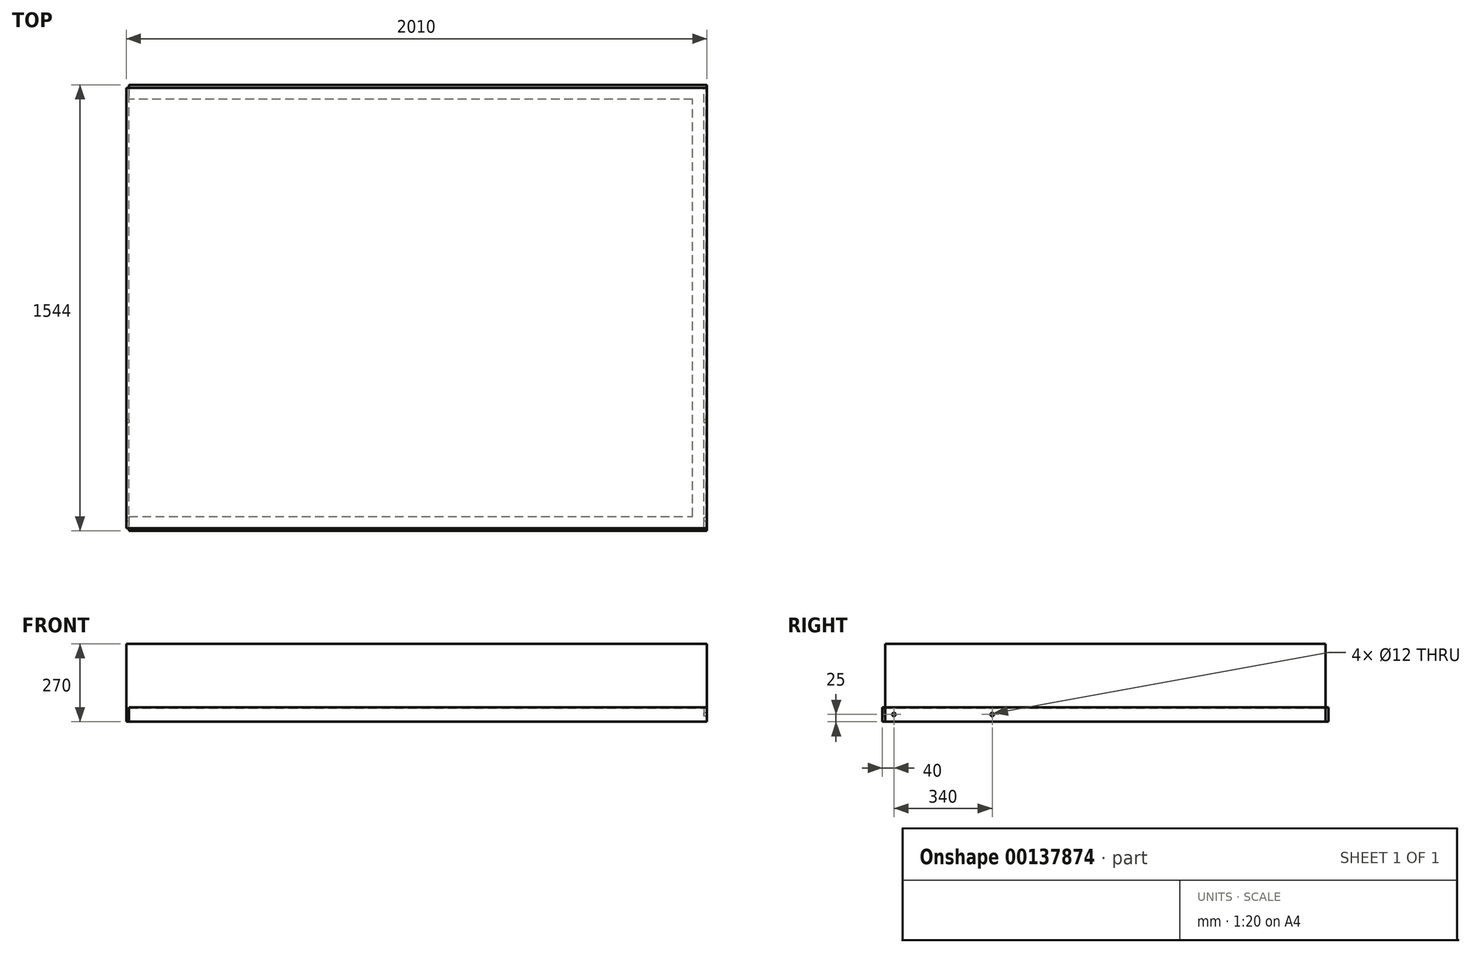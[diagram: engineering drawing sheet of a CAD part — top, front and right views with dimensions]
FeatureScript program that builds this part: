
annotation { "Feature Type Name" : "Feature", "Feature Type Description" : "" }
export const myFeature = defineFeature(function(context is Context, id is Id, definition is map)
    precondition{}
    {
        {
            var Q0;
            Q0=qCreatedBy(makeId("Top.planeOp"),FACE);
            var sketch = newSketch(context, id + "F0", { "sketchPlane" : qUnion([Q0])});
            skLineSegment(sketch, "E0.bottom", {"start": v(0, 0) * mm, "end": v(-2000, 0) * mm});
            skLineSegment(sketch, "E0.top", {"start": v(0, 1524) * mm, "end": v(-2000, 1524) * mm});
            skLineSegment(sketch, "E0.left", {"start": v(0, 0) * mm, "end": v(0, 1524) * mm});
            skLineSegment(sketch, "E0.right", {"start": v(-2000, 0) * mm, "end": v(-2000, 1524) * mm});
            skSolve(sketch);
        }
        {
            var Q0;
            Q0 = qSketchRegion(id + "F0", true);
            extrude(context, id + "F1", {"entities" : qUnion([Q0]), "depth" : 220 * mm});
        }
        {
            var Q0;
            Q0=makeQuery(id+"F1.opExtrude","SWEPT_FACE",FACE,{"disambiguationData":[OSD([sQuery(id+"F0.wireOp",EDGE,"E0.left")])]});
            var sketch = newSketch(context, id + "F2", { "sketchPlane" : qUnion([Q0])});
            skLineSegment(sketch, "E1", {"start": v(0, 220) * mm, "end": v(0, -50) * mm});
            skLineSegment(sketch, "E2", {"start": v(0, -50) * mm, "end": v(1524, -50) * mm});
            skLineSegment(sketch, "E3", {"start": v(1524, -50) * mm, "end": v(1524, 220) * mm});
            skLineSegment(sketch, "E4", {"start": v(1524, 220) * mm, "end": v(0, 220) * mm});
            skSolve(sketch);
        }
        {
            var Q0;
            Q0 = qSketchRegion(id + "F2", true);
            extrude(context, id + "F3", {"entities" : qUnion([Q0]), "operationType" : NewBodyOperationType.ADD, "oppositeDirection" : true, "depth" : 10 * mm});
        }
        {
            var Q0;
            Q0=makeQuery(id+"F1.opExtrude","SWEPT_FACE",FACE,{"disambiguationData":[OSD([sQuery(id+"F0.wireOp",EDGE,"E0.right")])]});
            var sketch = newSketch(context, id + "F4", { "sketchPlane" : qUnion([Q0])});
            skLineSegment(sketch, "E5", {"start": v(-1524, 220) * mm, "end": v(-1524, -50) * mm});
            skLineSegment(sketch, "E6", {"start": v(-1524, -50) * mm, "end": v(0, -50) * mm});
            skLineSegment(sketch, "E7", {"start": v(0, -50) * mm, "end": v(0, 220) * mm});
            skLineSegment(sketch, "E8", {"start": v(0, 220) * mm, "end": v(-1524, 220) * mm});
            skSolve(sketch);
        }
        {
            var Q0;
            Q0 = qSketchRegion(id + "F4", true);
            extrude(context, id + "F5", {"entities" : qUnion([Q0]), "operationType" : NewBodyOperationType.ADD, "depth" : 10 * mm});
        }
        {
            var Q0;
            Q0=makeQuery(id+"F3.boolean.opBoolean","MERGE",FACE,{"derivedFrom":[makeQuery(id+"F1.opExtrude","SWEPT_FACE",FACE,{"disambiguationData":[OSD([sQuery(id+"F0.wireOp",EDGE,"E0.left")])]}),makeQuery(id+"F3.opExtrude","CAP_FACE",FACE,{"disambiguationData":[OSD([sQuery(id+"F2.wireOp",EDGE,"E1"),sQuery(id+"F2.wireOp",EDGE,"E2"),sQuery(id+"F2.wireOp",EDGE,"E3"),sQuery(id+"F2.wireOp",EDGE,"E4")])],"isStart":true})]});
            var sketch = newSketch(context, id + "F6", { "sketchPlane" : qUnion([Q0])});
            skPoint(sketch, "E9", {"position": v(30, -25) * mm});
            skPoint(sketch, "E10", {"position": v(370, -25) * mm});
            skSolve(sketch);
        }
        {
            var Q0;
            Q0=sQuery(id+"F6.wireOp",VERTEX,"E9");
            var Q1;
            Q1=makeQuery(id+"F1.opExtrude","SWEPT_BODY",BODY,{"disambiguationData":[OSD([sQuery(id+"F0.wireOp",EDGE,"E0.bottom"),sQuery(id+"F0.wireOp",EDGE,"E0.top"),sQuery(id+"F0.wireOp",EDGE,"E0.left"),sQuery(id+"F0.wireOp",EDGE,"E0.right")])]});
            hole(context, id + "F7", {"style" : HoleStyle.SIMPLE, "endStyle" : HoleEndStyle.THROUGH, "holeDiameter" : 12 * mm, "locations" : qUnion([Q0]), "scope" : qUnion([Q1]), "isTappedThrough" : true, "startStyle" : HoleStartStyle.PART});
        }
        {
            var Q0;
            Q0=sQuery(id+"F6.wireOp",VERTEX,"E10");
            var Q1;
            Q1=makeQuery(id+"F1.opExtrude","SWEPT_BODY",BODY,{"disambiguationData":[OSD([sQuery(id+"F0.wireOp",EDGE,"E0.bottom"),sQuery(id+"F0.wireOp",EDGE,"E0.top"),sQuery(id+"F0.wireOp",EDGE,"E0.left"),sQuery(id+"F0.wireOp",EDGE,"E0.right")])]});
            hole(context, id + "F8", {"style" : HoleStyle.SIMPLE, "endStyle" : HoleEndStyle.THROUGH, "holeDiameter" : 12 * mm, "locations" : qUnion([Q0]), "scope" : qUnion([Q1]), "isTappedThrough" : true, "startStyle" : HoleStartStyle.PART});
        }
        {
            var Q0;
            Q0=qCreatedBy(makeId("Front.planeOp"),FACE);
            var sketch = newSketch(context, id + "F9", { "sketchPlane" : qUnion([Q0])});
            skLineSegment(sketch, "E11", {"start": v(0, 0) * mm, "end": v(-50, 0) * mm});
            skLineSegment(sketch, "E12", {"start": v(-50, 0) * mm, "end": v(-50, -3) * mm});
            skLineSegment(sketch, "E13", {"start": v(-50, -3) * mm, "end": v(-3, -3) * mm});
            skLineSegment(sketch, "E14", {"start": v(-3, -3) * mm, "end": v(-3, -50) * mm});
            skLineSegment(sketch, "E15", {"start": v(-3, -50) * mm, "end": v(0, -50) * mm});
            skLineSegment(sketch, "E16", {"start": v(0, -50) * mm, "end": v(0, 0) * mm});
            skSolve(sketch);
        }
        {
            var Q0;
            Q0 = qSketchRegion(id + "F9", true);
            var Q1;
            Q1=makeQuery(id+"F3.boolean.opBoolean","INTERSECT",EDGE,{"derivedFrom":[makeQuery(id+"F1.opExtrude","CAP_FACE",FACE,{"disambiguationData":[OSD([sQuery(id+"F0.wireOp",EDGE,"E0.bottom"),sQuery(id+"F0.wireOp",EDGE,"E0.top"),sQuery(id+"F0.wireOp",EDGE,"E0.left"),sQuery(id+"F0.wireOp",EDGE,"E0.right")])],"isStart":true}),makeQuery(id+"F3.opExtrude","CAP_FACE",FACE,{"disambiguationData":[OSD([sQuery(id+"F2.wireOp",EDGE,"E1"),sQuery(id+"F2.wireOp",EDGE,"E2"),sQuery(id+"F2.wireOp",EDGE,"E3"),sQuery(id+"F2.wireOp",EDGE,"E4")])],"isStart":false})]});
            var Q2;
            Q2=makeQuery(id+"F1.opExtrude","CAP_EDGE",EDGE,{"disambiguationData":[OSD([sQuery(id+"F0.wireOp",EDGE,"E0.top")])],"isStart":true});
            var Q3;
            Q3=makeQuery(id+"F1.opExtrude","CAP_EDGE",EDGE,{"disambiguationData":[OSD([sQuery(id+"F0.wireOp",EDGE,"E0.right")])],"isStart":true});
            var Q4;
            Q4=makeQuery(id+"F1.opExtrude","CAP_EDGE",EDGE,{"disambiguationData":[OSD([sQuery(id+"F0.wireOp",EDGE,"E0.bottom")])],"isStart":true});
            sweep(context, id + "F10", {"profiles" : qUnion([Q0]), "path" : qUnion([Q1, Q2, Q3, Q4])});
        }
    });
